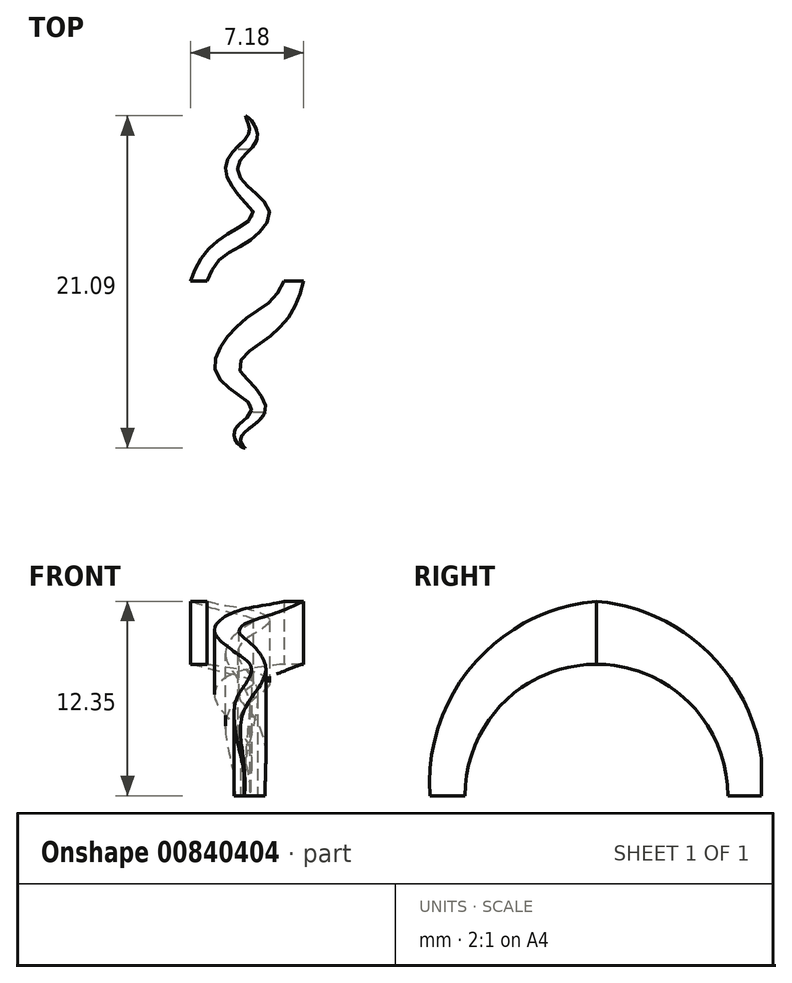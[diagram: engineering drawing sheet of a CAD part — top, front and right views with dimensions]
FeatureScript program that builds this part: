
annotation { "Feature Type Name" : "Feature", "Feature Type Description" : "" }
export const myFeature = defineFeature(function(context is Context, id is Id, definition is map)
    precondition{}
    {
        {
            var Q0;
            Q0=qCreatedBy(makeId("Front.planeOp"),FACE);
            var sketch = newSketch(context, id + "F0", { "sketchPlane" : qUnion([Q0])});
            skLineSegment(sketch, "E0", {"start": v(0, 8.35) * mm, "end": v(-1.2, 8.35) * mm});
            skLineSegment(sketch, "E1", {"start": v(-1.2, 8.35) * mm, "end": v(-1.2, 10.35) * mm});
            skLineSegment(sketch, "E2", {"start": v(1.2, 10.35) * mm, "end": v(1.2, 8.35) * mm});
            skLineSegment(sketch, "E3", {"start": v(1.2, 8.35) * mm, "end": v(0, 8.35) * mm});
            skArc(sketch, "E4", {"start": v(1.2, 10.35) * mm, "mid": v(0, 10.56) * mm, "end": v(-1.2, 10.35) * mm});
            skSolve(sketch);
        }
        {
            var Q0;
            Q0=qCreatedBy(makeId("Top.planeOp"),FACE);
            var sketch = newSketch(context, id + "F1", { "sketchPlane" : qUnion([Q0])});
            skLineSegment(sketch, "E5", {"start": v(0, 0) * mm, "end": v(12.97, 0) * mm});
            skSolve(sketch);
        }
        {
            var Q0;
            Q0=makeQuery(id+"F0.imprint","IMPRINT",FACE,{"disambiguationData":[TD([[makeQuery(id+"F0.imprint","IMPRINT",EDGE,{"derivedFrom":sQuery(id+"F0.wireOp",EDGE,"E0")}),-1.0]])]});
            var Q1;
            Q1=sQuery(id+"F1.wireOp",EDGE,"E5");
            revolve(context, id + "F2", {"surfaceOperationType" : NewSurfaceOperationType.NEW, "entities" : qUnion([Q0]), "axis" : qUnion([Q1]), "revolveType" : RevolveType.FULL});
        }
        {
            var Q0;
            Q0=qCreatedBy(makeId("Right.planeOp"),FACE);
            var sketch = newSketch(context, id + "F3", { "sketchPlane" : qUnion([Q0])});
            skLineSegment(sketch, "E6", {"start": v(-8.35, 0) * mm, "end": v(-10.56, 0) * mm});
            skLineSegment(sketch, "E7", {"start": v(8.35, 0) * mm, "end": v(10.57, 0) * mm});
            skArc(sketch, "E8", {"start": v(0, 12.35) * mm, "mid": v(-7.81, 8.34) * mm, "end": v(-10.56, 0) * mm});
            skArc(sketch, "E9", {"start": v(10.57, 0) * mm, "mid": v(7.82, 8.35) * mm, "end": v(0, 12.35) * mm});
            skArc(sketch, "E10", {"start": v(8.35, 0) * mm, "mid": v(0, 8.35) * mm, "end": v(-8.35, 0) * mm});
            skSolve(sketch);
        }
        {
            var Q0;
            Q0 = qSketchRegion(id + "F3", true);
            extrude(context, id + "F4", {"entities" : qUnion([Q0]), "operationType" : NewBodyOperationType.ADD, "depth" : 4 * mm, "offsetDistance" : 25 * mm, "hasSecondDirection" : true, "secondDirectionOppositeDirection" : true, "secondDirectionDepth" : 4 * mm});
        }
        {
            var Q0;
            Q0=qCreatedBy(makeId("Top.planeOp"),FACE);
            var sketch = newSketch(context, id + "F5", { "sketchPlane" : qUnion([Q0])});
            skFitSpline(sketch, "E11", {"points": [v(-3.5, 0) * mm, v(-2.25, 2.17) * mm, v(0, 3.68) * mm, v(0.51, 4.26) * mm, v(0, 4.97) * mm, v(-1.28, 7.3) * mm, v(0, 9.03) * mm, v(0.23, 9.73) * mm, v(0, 10.5) * mm, v(0, 10.6) * mm], "startDerivative": vector(5.04, 14.6) * mm, "endDerivative": vector(0.65, 2.02) * mm});
            skFitSpline(sketch, "E12", {"points": [v(3.68, 0) * mm, v(1.6, -3.48) * mm, v(0, -4.63) * mm, v(-0.43, -5.43) * mm, v(0, -6.14) * mm, v(1.27, -8.16) * mm, v(0, -9.54) * mm, v(-0.32, -10.02) * mm, v(0, -10.63) * mm], "startDerivative": vector(-5.86, -26.14) * mm, "endDerivative": vector(11.78, -10.16) * mm});
            skFitSpline(sketch, "E13", {"points": [v(-2.45, 0) * mm, v(-1.32, 1.64) * mm, v(0, 2.4) * mm, v(1.52, 4.32) * mm, v(0, 6.16) * mm, v(-0.5, 7.27) * mm, v(0, 8.1) * mm, v(0.74, 9.04) * mm, v(0, 10.5) * mm], "startDerivative": vector(7.28, 19.9) * mm, "endDerivative": vector(-12.78, 7.78) * mm});
            skFitSpline(sketch, "E14", {"points": [v(2.45, 0) * mm, v(1.38, -1.45) * mm, v(0, -2.4) * mm, v(-1.97, -5.53) * mm, v(0, -7.55) * mm, v(0.37, -8.1) * mm, v(0, -8.74) * mm, v(-0.68, -9.45) * mm, v(0, -10.63) * mm], "startDerivative": vector(-5.77, -14.13) * mm, "endDerivative": vector(19.07, -7.88) * mm});
            skLineSegment(sketch, "E15", {"start": v(-2.45, 0) * mm, "end": v(0, 0) * mm});
            skLineSegment(sketch, "E16", {"start": v(0, 0) * mm, "end": v(2.45, 0) * mm});
            skLineSegment(sketch, "E17", {"start": v(-3.5, 0) * mm, "end": v(-2.45, 0) * mm});
            skLineSegment(sketch, "E18", {"start": v(3.68, 0) * mm, "end": v(2.45, 0) * mm});
            skLineSegment(sketch, "E19", {"start": v(-2.45, 0) * mm, "end": v(-3.5, 0) * mm});
            skSolve(sketch);
        }
        {
            var Q0;
            Q0 = qSketchRegion(id + "F5", true);
            extrude(context, id + "F6", {"entities" : qUnion([Q0]), "operationType" : NewBodyOperationType.INTERSECT, "depth" : 25 * mm, "offsetDistance" : 25 * mm});
        }
    });
